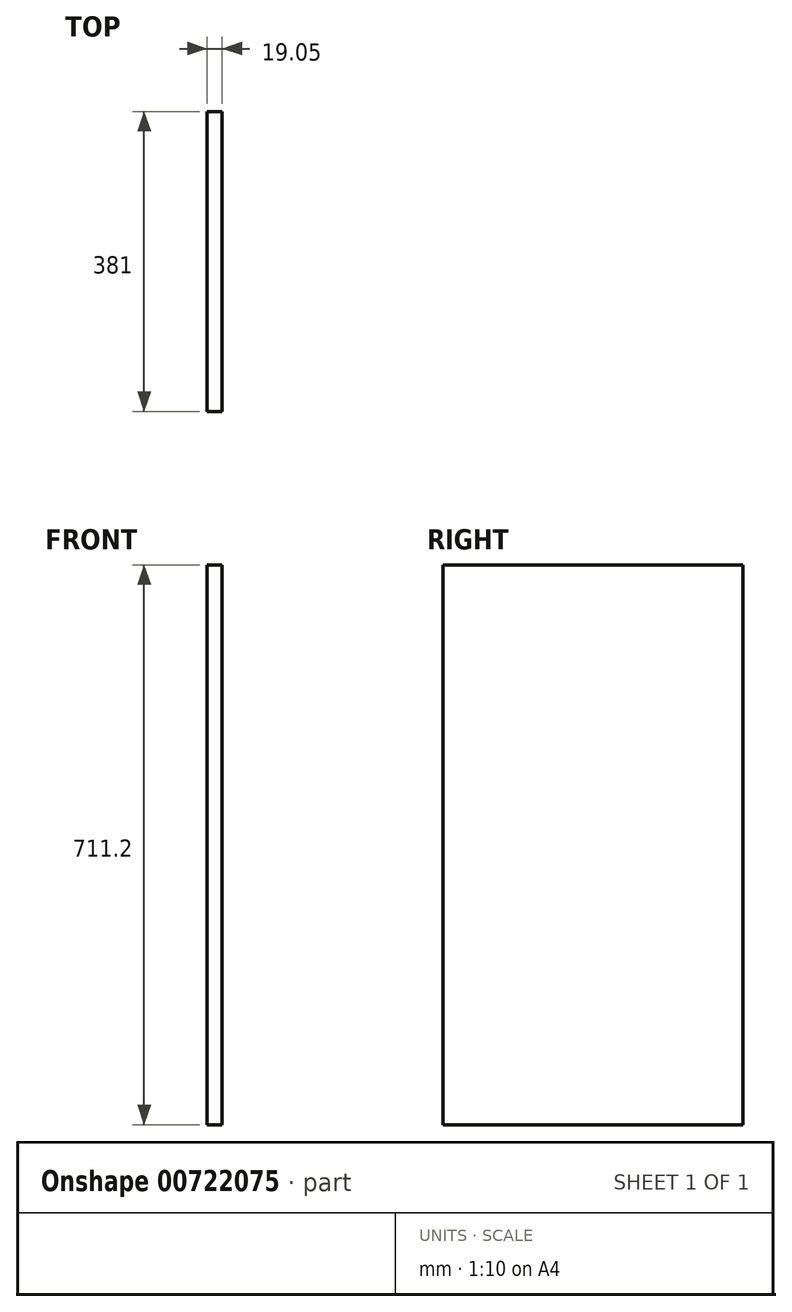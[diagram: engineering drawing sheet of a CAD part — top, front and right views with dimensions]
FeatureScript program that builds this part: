
annotation { "Feature Type Name" : "Feature", "Feature Type Description" : "" }
export const myFeature = defineFeature(function(context is Context, id is Id, definition is map)
    precondition{}
    {
        {
            var Q0;
            Q0=qCreatedBy(makeId("Right.planeOp"),FACE);
            var sketch = newSketch(context, id + "F0", { "sketchPlane" : qUnion([Q0])});
            skLineSegment(sketch, "E0.bottom", {"start": v(190.5, 355.6) * mm, "end": v(-190.5, 355.6) * mm});
            skLineSegment(sketch, "E0.top", {"start": v(190.5, -355.6) * mm, "end": v(-190.5, -355.6) * mm});
            skLineSegment(sketch, "E0.left", {"start": v(190.5, 355.6) * mm, "end": v(190.5, -355.6) * mm});
            skLineSegment(sketch, "E0.right", {"start": v(-190.5, 355.6) * mm, "end": v(-190.5, -355.6) * mm});
            skPoint(sketch, "E0.middle", {"position": v(0, 0) * mm});
            skSolve(sketch);
        }
        {
            var Q0;
            Q0=makeQuery(id+"F0.imprint","IMPRINT",FACE,{"disambiguationData":[TD([[makeQuery(id+"F0.imprint","IMPRINT",EDGE,{"derivedFrom":sQuery(id+"F0.wireOp",EDGE,"E0.bottom")}),1.0]])]});
            extrude(context, id + "F1", {"entities" : qUnion([Q0]), "depth" : 19.05 * mm, "offsetDistance" : 25.4 * mm});
        }
    });
